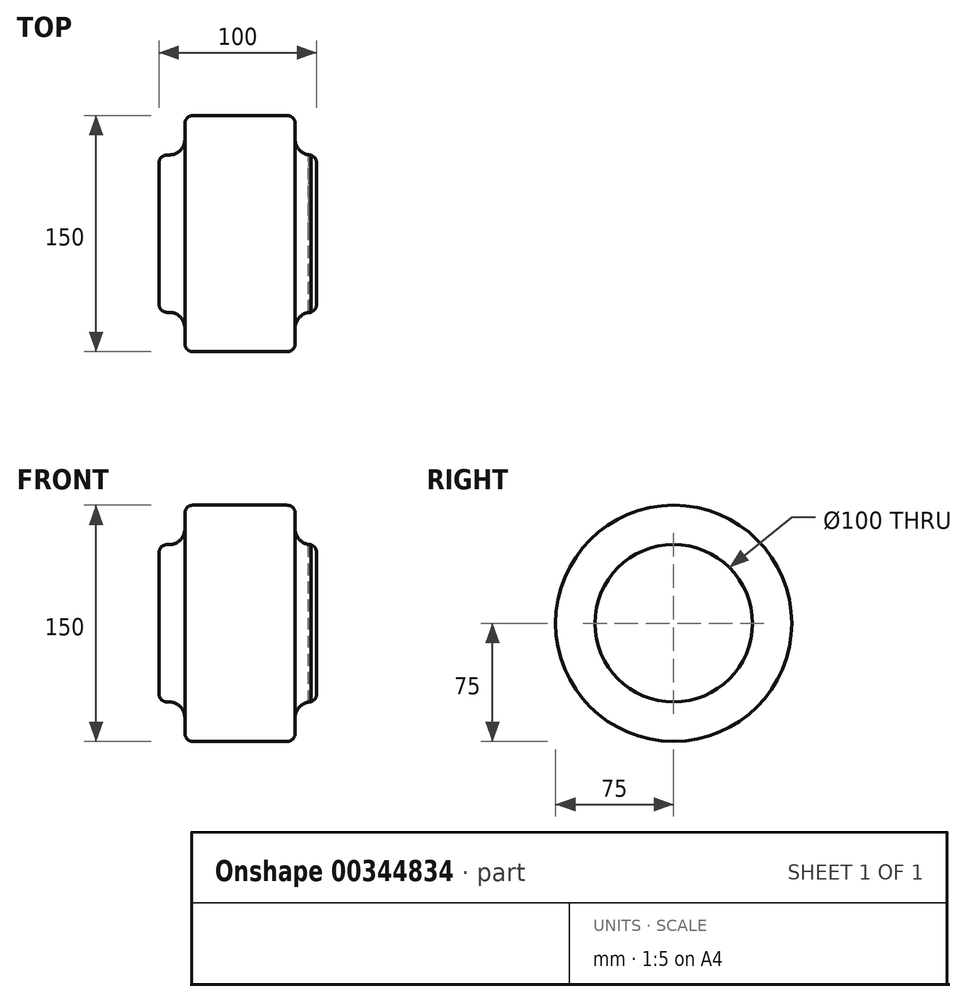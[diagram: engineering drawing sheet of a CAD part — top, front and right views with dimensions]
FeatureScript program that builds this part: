
annotation { "Feature Type Name" : "Feature", "Feature Type Description" : "" }
export const myFeature = defineFeature(function(context is Context, id is Id, definition is map)
    precondition{}
    {
        {
            var Q0;
            Q0=qCreatedBy(makeId("Front.planeOp"),FACE);
            var sketch = newSketch(context, id + "F0", { "sketchPlane" : qUnion([Q0])});
            skLineSegment(sketch, "E0", {"start": v(-51.38, 0) * mm, "end": v(-51.38, 45) * mm});
            skLineSegment(sketch, "E1", {"start": v(-46.38, 50) * mm, "end": v(-45, 50) * mm});
            skLineSegment(sketch, "E2", {"start": v(-35, 60) * mm, "end": v(-35, 70) * mm});
            skLineSegment(sketch, "E3", {"start": v(-30, 75) * mm, "end": v(30, 75) * mm});
            skLineSegment(sketch, "E4", {"start": v(35, 70) * mm, "end": v(35, 60) * mm});
            skLineSegment(sketch, "E5", {"start": v(43.62, 50) * mm, "end": v(45, 50) * mm});
            skLineSegment(sketch, "E6", {"start": v(48.62, 45) * mm, "end": v(48.62, 0) * mm});
            skLineSegment(sketch, "E7", {"start": v(48.62, 0) * mm, "end": v(-51.38, 0) * mm});
            skPoint(sketch, "E8.visualSharp", {"position": v(-51.38, 50) * mm});
            skArc(sketch, "E8.filletArc", {"start": v(-46.38, 50) * mm, "mid": v(-49.91, 48.54) * mm, "end": v(-51.38, 45) * mm});
            skPoint(sketch, "E9.visualSharp", {"position": v(-35, 75) * mm});
            skArc(sketch, "E9.filletArc", {"start": v(-30, 75) * mm, "mid": v(-33.54, 73.54) * mm, "end": v(-35, 70) * mm});
            skPoint(sketch, "E10.visualSharp", {"position": v(35, 75) * mm});
            skArc(sketch, "E10.filletArc", {"start": v(35, 70) * mm, "mid": v(33.54, 73.54) * mm, "end": v(30, 75) * mm});
            skPoint(sketch, "E11.visualSharp", {"position": v(48.62, 50) * mm});
            skArc(sketch, "E11.filletArc", {"start": v(48.62, 45) * mm, "mid": v(47.16, 48.54) * mm, "end": v(43.62, 50) * mm});
            skPoint(sketch, "E12.visualSharp", {"position": v(-35, 50) * mm});
            skArc(sketch, "E12.filletArc", {"start": v(-45, 50) * mm, "mid": v(-37.93, 52.93) * mm, "end": v(-35, 60) * mm});
            skPoint(sketch, "E13.visualSharp", {"position": v(35, 50) * mm});
            skArc(sketch, "E13.filletArc", {"start": v(35, 60) * mm, "mid": v(37.93, 52.93) * mm, "end": v(45, 50) * mm});
            skSolve(sketch);
        }
        {
            var Q0;
            Q0=makeQuery(id+"F0.imprint","IMPRINT",FACE,{"disambiguationData":[TD([[makeQuery(id+"F0.imprint","IMPRINT",EDGE,{"derivedFrom":sQuery(id+"F0.wireOp",EDGE,"E0")}),-1.0]])]});
            var Q1;
            Q1=sQuery(id+"F0.wireOp",EDGE,"E7");
            revolve(context, id + "F1", {"entities" : qUnion([Q0]), "axis" : qUnion([Q1]), "revolveType" : RevolveType.FULL});
        }
    });
